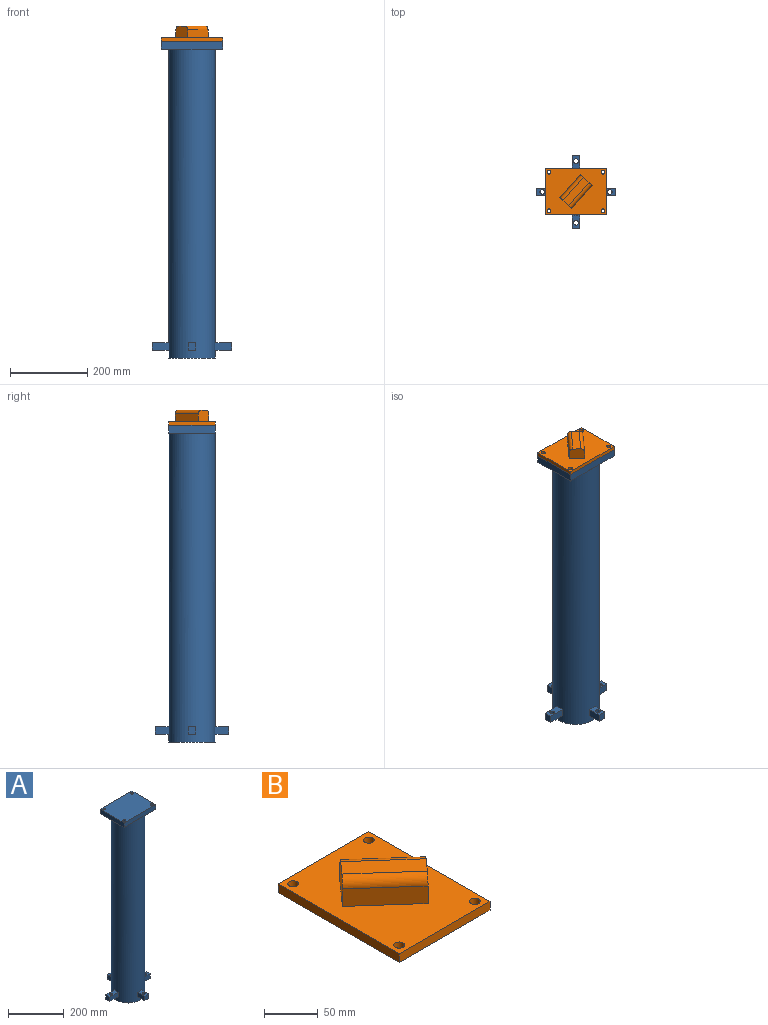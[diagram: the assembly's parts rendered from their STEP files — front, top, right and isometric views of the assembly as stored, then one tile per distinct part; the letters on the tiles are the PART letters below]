
ASSEMBLY  parts=2 mates=1
PART A: 37 faces, bbox 205x190x820 mm
  f0: plane 120x80mm, normal (0,0,-1), area 3788.1mm2, adj f1,f2,f6,f7,f8,f11
  f1: plane 120x20mm, normal (-1,0,0), area 2400mm2, adj f0,f2,f7,f9
  f2: plane 160x20mm, normal (0,-1,0), area 3200mm2, adj f0,f1,f3,f9,f10
  f3: plane 120x20mm, normal (1,0,0), area 2400mm2, adj f2,f7,f9,f10
  f4: cylinder r=5mm len=20mm, axis (0,0,-1), area 628.3mm2, adj f9,f10
  f5: cylinder r=5mm len=20mm, axis (0,0,-1), area 628.3mm2, adj f9,f10
  f6: cylinder r=5mm len=20mm, axis (0,0,-1), area 628.3mm2, adj f0,f9
  f7: plane 160x20mm, normal (0,1,0), area 3200mm2, adj f0,f1,f3,f9,f10
  f8: cylinder r=5mm len=20mm, axis (0,0,-1), area 628.3mm2, adj f0,f9
  f9: plane 160x120mm, normal (0,0,1), area 18885.8mm2, adj f1,f2,f3,f4,f5,f6,f7,f8
  f10: plane 120x80mm, normal (0,0,-1), area 3788.1mm2, adj f2,f3,f4,f5,f7,f11
  f11: cylinder r=60mm len=800mm, axis (0,0,1), area 299985.4mm2, adj f0,f10,f12,f14,f15,f16,f17,f18
  f12: plane 120x120mm, normal (0,0,-1), area 11309.7mm2, adj f11
  f13: plane 20x20mm, normal (0,-1,0), area 400mm2, adj f14,f15,f16,f17
  f14: plane 35.84x20mm, normal (-1,0,0), area 716.8mm2, adj f11,f13,f16,f17
  f15: plane 35.84x20mm, normal (1,0,0), area 716.8mm2, adj f11,f13,f16,f17
  f16: plane 35.84x20mm, normal (0,0,-1), area 592.5mm2, adj f11,f13,f14,f15,f36
  f17: plane 35.84x20mm, normal (0,0,1), area 592.5mm2, adj f11,f13,f14,f15,f36
  f18: plane 35.84x20mm, normal (1,0,0), area 716.8mm2, adj f11,f20,f21,f22
  f19: plane 35.84x20mm, normal (-1,0,0), area 716.8mm2, adj f11,f20,f21,f22
  f20: plane 20x20mm, normal (0,1,0), area 400mm2, adj f18,f19,f21,f22
  f21: plane 35.84x20mm, normal (0,0,1), area 592.5mm2, adj f11,f18,f19,f20,f35
  f22: plane 35.84x20mm, normal (0,0,-1), area 592.5mm2, adj f11,f18,f19,f20,f35
  f23: plane 20x20mm, normal (-1,0,0), area 400mm2, adj f24,f25,f26,f27
  f24: plane 43.34x20mm, normal (0,-1,0), area 866.8mm2, adj f11,f23,f26,f27
  f25: plane 43.34x20mm, normal (0,1,0), area 866.8mm2, adj f11,f23,f26,f27
  f26: plane 43.34x20mm, normal (0,0,-1), area 742.5mm2, adj f11,f23,f24,f25,f34
  f27: plane 43.34x20mm, normal (0,0,1), area 742.5mm2, adj f11,f23,f24,f25,f34
  f28: plane 43.34x20mm, normal (0,0,-1), area 742.5mm2, adj f11,f29,f30,f32,f33
  f29: plane 43.34x20mm, normal (0,-1,0), area 866.8mm2, adj f11,f28,f31,f32
  f30: plane 43.34x20mm, normal (0,1,0), area 866.8mm2, adj f11,f28,f31,f32
  f31: plane 43.34x20mm, normal (0,0,1), area 742.5mm2, adj f11,f29,f30,f32,f33
  f32: plane 20x20mm, normal (1,0,0), area 400mm2, adj f28,f29,f30,f31
  f33: cylinder r=6mm len=20mm, axis (0,0,1), area 754mm2, adj f28,f31
  f34: cylinder r=6mm len=20mm, axis (0,0,1), area 754mm2, adj f26,f27
  f35: cylinder r=6mm len=20mm, axis (0,0,1), area 754mm2, adj f21,f22
  f36: cylinder r=6mm len=20mm, axis (0,0,1), area 754mm2, adj f16,f17
PART B: 17 faces, bbox 120x160x40 mm
  f0: plane 30x29.92mm, normal (-0.75,0.66,0), area 1157.1mm2, adj f1,f3,f4,f13,f15,f16
  f1: plane 59.83x53.11mm, normal (-0.66,-0.75,0), area 1600mm2, adj f0,f2,f13,f15
  f2: plane 30x29.92mm, normal (0.75,-0.66,0), area 1157.1mm2, adj f1,f3,f4,f13,f15,f16
  f3: plane 59.83x53.11mm, normal (0.66,0.75,0), area 1600mm2, adj f0,f2,f13,f16
  f4: plane 73.11x68.06mm, normal (0,0,1), area 1600mm2, adj f0,f2,f15,f16
  f5: plane 160x10mm, normal (-1,0,0), area 1600mm2, adj f6,f8,f13,f14
  f6: plane 120x10mm, normal (0,-1,0), area 1200mm2, adj f5,f7,f13,f14
  f7: plane 160x10mm, normal (1,0,0), area 1600mm2, adj f6,f8,f13,f14
  f8: plane 120x10mm, normal (0,1,0), area 1200mm2, adj f5,f7,f13,f14
  f9: cylinder r=5mm len=10mm, axis (0,0,-1), area 314.2mm2, adj f13,f14
  f10: cylinder r=5mm len=10mm, axis (0,0,-1), area 314.2mm2, adj f13,f14
  f11: cylinder r=5mm len=10mm, axis (0,0,-1), area 314.2mm2, adj f13,f14
  f12: cylinder r=5mm len=10mm, axis (0,0,-1), area 314.2mm2, adj f13,f14
  f13: plane 160x120mm, normal (0,0,1), area 15685.8mm2, adj f0,f1,f2,f3,f5,f6,f7,f8
  f14: plane 160x120mm, normal (0,0,-1), area 18885.8mm2, adj f5,f6,f7,f8,f9,f10,f11,f12
  f15: cylinder r=10mm len=66.47mm, axis (-0.75,0.66,0), area 1256.6mm2, adj f0,f1,f2,f4
  f16: cylinder r=10mm len=66.47mm, axis (0.75,-0.66,0), area 1256.6mm2, adj f0,f2,f3,f4
PLACE A at identity
PLACE B rot(axis=(0,0,1),90deg) t=(0,0,20)mm
MATE fastened B.f14 <-> A.f11  axis (0,0,-1) through (0,0,20)mm
